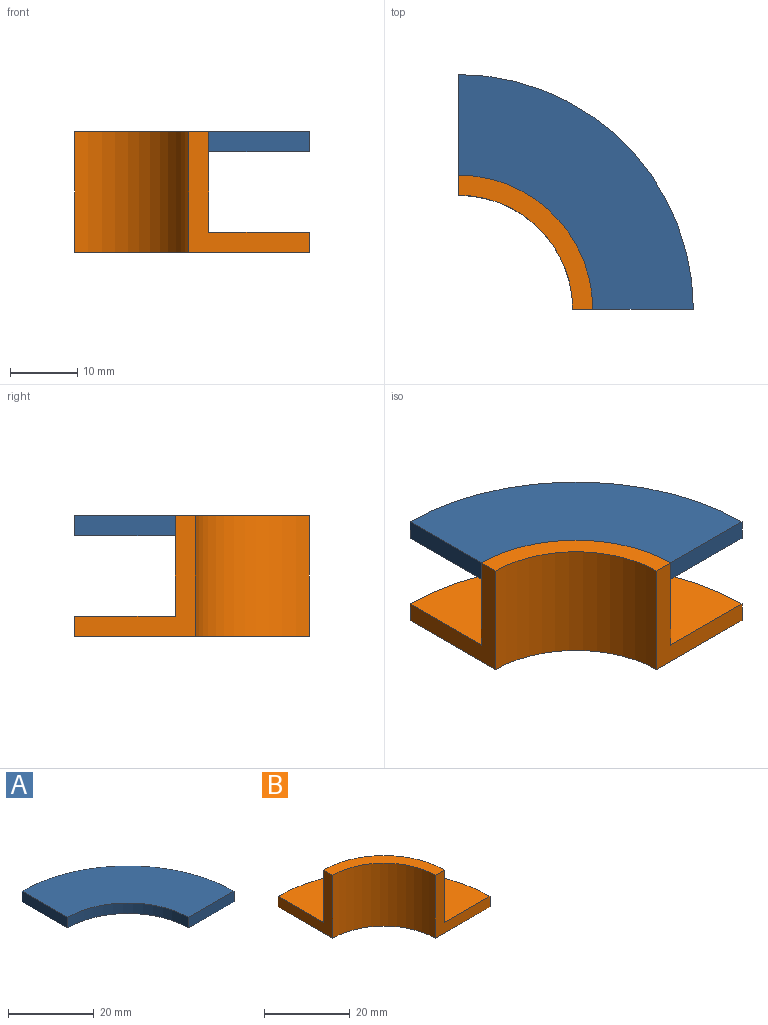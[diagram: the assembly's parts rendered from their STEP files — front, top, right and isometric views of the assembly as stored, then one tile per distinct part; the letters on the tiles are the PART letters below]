
ASSEMBLY  parts=2 mates=1
PART A: 6 faces, bbox 35x35x3 mm
  f0: cylinder r=20mm len=20mm, axis (0,0,-1), area 94.2mm2, adj f1,f3,f4,f5
  f1: plane 15x3mm, normal (0,-1,0), area 45mm2, adj f0,f2,f4,f5
  f2: cylinder r=35mm len=35mm, axis (0,0,-1), area 164.9mm2, adj f1,f3,f4,f5
  f3: plane 15x3mm, normal (-1,0,0), area 45mm2, adj f0,f2,f4,f5
  f4: plane 35x35mm, normal (0,0,1), area 648mm2, adj f0,f1,f2,f3
  f5: plane 35x35mm, normal (0,0,-1), area 648mm2, adj f0,f1,f2,f3
PART B: 8 faces, bbox 35x35x18 mm
  f0: plane 18x18mm, normal (0,-1,0), area 99mm2, adj f1,f3,f4,f5,f6,f7
  f1: cylinder r=35mm len=35mm, axis (0,0,-1), area 164.9mm2, adj f0,f2,f3,f4
  f2: plane 18x18mm, normal (-1,0,0), area 99mm2, adj f1,f3,f4,f5,f6,f7
  f3: plane 35x35mm, normal (0,0,1), area 648mm2, adj f0,f1,f2,f5
  f4: plane 35x35mm, normal (0,0,-1), area 735.1mm2, adj f0,f1,f2,f6
  f5: cylinder r=20mm len=20mm, axis (0,0,-1), area 471.2mm2, adj f0,f2,f3,f7
  f6: cylinder r=17mm len=18mm, axis (0,0,-1), area 480.7mm2, adj f0,f2,f4,f7
  f7: plane 20x20mm, normal (0,0,1), area 87.2mm2, adj f0,f2,f5,f6
PLACE A t=(-9.43,-6.58,22.89)mm
PLACE B t=(-9.43,-6.58,7.89)mm
MATE fastened A.f4 <-> B.f7  axis (0,0,1) through (10.57,-6.58,25.89)mm
